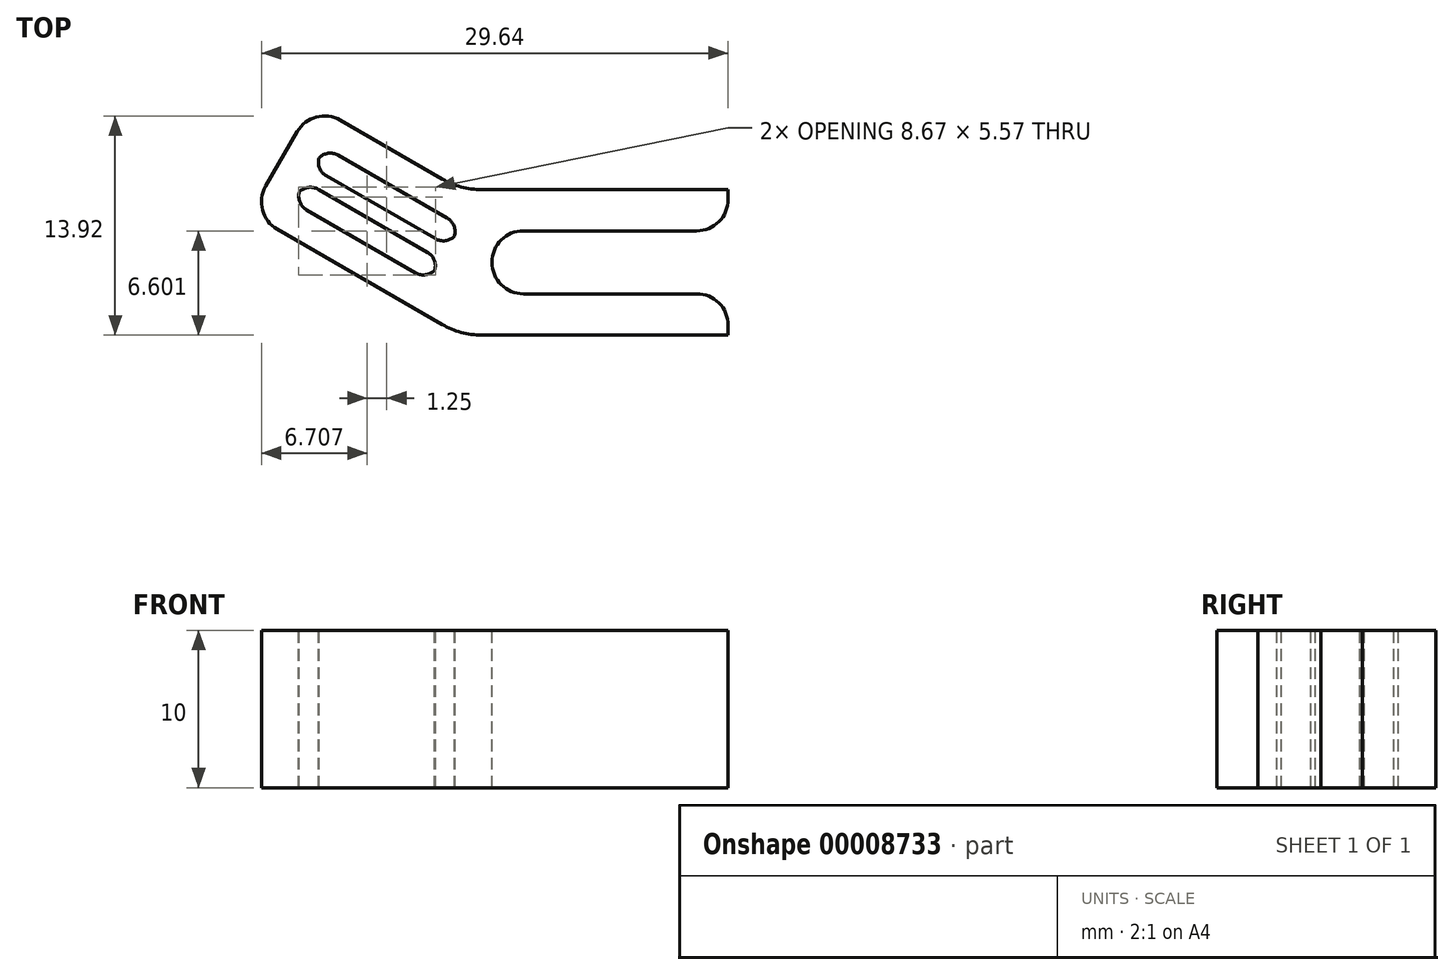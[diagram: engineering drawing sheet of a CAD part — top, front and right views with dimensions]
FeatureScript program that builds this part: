
annotation { "Feature Type Name" : "Feature", "Feature Type Description" : "" }
export const myFeature = defineFeature(function(context is Context, id is Id, definition is map)
    precondition{}
    {
        {
            var Q0;
            Q0=qCreatedBy(makeId("Top.planeOp"),FACE);
            var sketch = newSketch(context, id + "F0", { "sketchPlane" : qUnion([Q0])});
            skLineSegment(sketch, "E0", {"start": v(0, 0) * mm, "end": v(17, 0) * mm});
            skLineSegment(sketch, "E1", {"start": v(17, 0) * mm, "end": v(17, 2.62) * mm});
            skLineSegment(sketch, "E2", {"start": v(17, 2.62) * mm, "end": v(2, 2.62) * mm});
            skLineSegment(sketch, "E3", {"start": v(2, 2.62) * mm, "end": v(2, 6.62) * mm});
            skLineSegment(sketch, "E4", {"start": v(2, 6.62) * mm, "end": v(17, 6.62) * mm});
            skLineSegment(sketch, "E5", {"start": v(17, 6.62) * mm, "end": v(17, 9.24) * mm});
            skLineSegment(sketch, "E6", {"start": v(17, 9.24) * mm, "end": v(0, 9.24) * mm});
            skLineSegment(sketch, "E7", {"start": v(0, 9.24) * mm, "end": v(-9.37, 14.65) * mm});
            skLineSegment(sketch, "E8", {"start": v(-9.37, 14.65) * mm, "end": v(-13.37, 7.72) * mm});
            skLineSegment(sketch, "E9", {"start": v(-13.37, 7.72) * mm, "end": v(0, 0) * mm});
            skLineSegment(sketch, "E10", {"start": v(0.02, 6.92) * mm, "end": v(-8.64, 11.92) * mm});
            skLineSegment(sketch, "E11", {"start": v(-8.64, 11.92) * mm, "end": v(-9.39, 10.62) * mm});
            skLineSegment(sketch, "E12", {"start": v(-9.39, 10.62) * mm, "end": v(-0.73, 5.62) * mm});
            skLineSegment(sketch, "E13", {"start": v(-1.23, 4.75) * mm, "end": v(-9.89, 9.75) * mm});
            skLineSegment(sketch, "E14", {"start": v(-9.89, 9.75) * mm, "end": v(-10.64, 8.45) * mm});
            skLineSegment(sketch, "E15", {"start": v(-10.64, 8.45) * mm, "end": v(-1.98, 3.45) * mm});
            skLineSegment(sketch, "E16", {"start": v(-1.98, 3.45) * mm, "end": v(-1.23, 4.75) * mm});
            skLineSegment(sketch, "E17", {"start": v(-0.73, 5.62) * mm, "end": v(0.02, 6.92) * mm});
            skSolve(sketch);
        }
        {
            var Q0;
            Q0 = qSketchRegion(id + "F0", true);
            extrude(context, id + "F1", {"entities" : qUnion([Q0]), "depth" : 10 * mm});
        }
        {
            var Q0;
            Q0=makeQuery(id+"F1.opExtrude","SWEPT_EDGE",EDGE,{"disambiguationData":[OSD([sQuery(id+"F0.wireOp",EDGE,"22adb448-7b01-4dee-b25c-27ad3b814b58.bottom"),sQuery(id+"F0.wireOp",EDGE,"5c2d3520-68a2-4204-9db6-72b257983ef0")])]});
            var Q1;
            Q1=makeQuery(id+"F1.opExtrude","SWEPT_EDGE",EDGE,{"disambiguationData":[OSD([sQuery(id+"F0.wireOp",EDGE,"22adb448-7b01-4dee-b25c-27ad3b814b58.top"),sQuery(id+"F0.wireOp",EDGE,"5c2d3520-68a2-4204-9db6-72b257983ef0")])]});
            var Q2;
            Q2=makeQuery(id+"F1.opExtrude","SWEPT_EDGE",EDGE,{"disambiguationData":[OSD([sQuery(id+"F0.wireOp",EDGE,"22adb448-7b01-4dee-b25c-27ad3b814b58.bottom"),sQuery(id+"F0.wireOp",EDGE,"22adb448-7b01-4dee-b25c-27ad3b814b58.left")])]});
            var Q3;
            Q3=makeQuery(id+"F1.opExtrude","SWEPT_EDGE",EDGE,{"disambiguationData":[OSD([sQuery(id+"F0.wireOp",EDGE,"22adb448-7b01-4dee-b25c-27ad3b814b58.top"),sQuery(id+"F0.wireOp",EDGE,"22adb448-7b01-4dee-b25c-27ad3b814b58.left")])]});
            var Q4;
            Q4=makeQuery(id+"F1.opExtrude","SWEPT_EDGE",EDGE,{"disambiguationData":[OSD([sQuery(id+"F0.wireOp",EDGE,"E2"),sQuery(id+"F0.wireOp",EDGE,"E3")])]});
            var Q5;
            Q5=makeQuery(id+"F1.opExtrude","SWEPT_EDGE",EDGE,{"disambiguationData":[OSD([sQuery(id+"F0.wireOp",EDGE,"E3"),sQuery(id+"F0.wireOp",EDGE,"E4")])]});
            var Q6;
            Q6=makeQuery(id+"F1.opExtrude","SWEPT_EDGE",EDGE,{"disambiguationData":[OSD([sQuery(id+"F0.wireOp",EDGE,"E1"),sQuery(id+"F0.wireOp",EDGE,"E2")])]});
            var Q7;
            Q7=makeQuery(id+"F1.opExtrude","SWEPT_EDGE",EDGE,{"disambiguationData":[OSD([sQuery(id+"F0.wireOp",EDGE,"E4"),sQuery(id+"F0.wireOp",EDGE,"E5")])]});
            var Q8;
            Q8=makeQuery(id+"F1.opExtrude","SWEPT_EDGE",EDGE,{"disambiguationData":[OSD([sQuery(id+"F0.wireOp",EDGE,"c99527b5-ed65-49ce-9ce6-7f1a6e514e39"),sQuery(id+"F0.wireOp",EDGE,"0ae14092-fb47-4e55-a7a5-957fbf246e4f")])]});
            var Q9;
            Q9=makeQuery(id+"F1.opExtrude","SWEPT_EDGE",EDGE,{"disambiguationData":[OSD([sQuery(id+"F0.wireOp",EDGE,"6eeee744-6f9b-4a90-b979-4488c1a42c6f"),sQuery(id+"F0.wireOp",EDGE,"0ae14092-fb47-4e55-a7a5-957fbf246e4f")])]});
            var Q10;
            Q10=makeQuery(id+"F1.opExtrude","SWEPT_EDGE",EDGE,{"disambiguationData":[OSD([sQuery(id+"F0.wireOp",EDGE,"E7"),sQuery(id+"F0.wireOp",EDGE,"E8")])]});
            var Q11;
            Q11=makeQuery(id+"F1.opExtrude","SWEPT_EDGE",EDGE,{"disambiguationData":[OSD([sQuery(id+"F0.wireOp",EDGE,"E8"),sQuery(id+"F0.wireOp",EDGE,"E9")])]});
            fillet(context, id + "F2", {"entities" : qUnion([Q0, Q1, Q2, Q3, Q4, Q5, Q6, Q7, Q8, Q9, Q10, Q11]), "radius" : 2 * mm, "tangentPropagation" : true, "allowEdgeOverflow" : false});
        }
        {
            var Q0;
            Q0=makeQuery(id+"F1.opExtrude","SWEPT_EDGE",EDGE,{"disambiguationData":[OSD([sQuery(id+"F0.wireOp",EDGE,"E14"),sQuery(id+"F0.wireOp",EDGE,"E15")])]});
            var Q1;
            Q1=makeQuery(id+"F1.opExtrude","SWEPT_EDGE",EDGE,{"disambiguationData":[OSD([sQuery(id+"F0.wireOp",EDGE,"E11"),sQuery(id+"F0.wireOp",EDGE,"E12")])]});
            var Q2;
            Q2=makeQuery(id+"F1.opExtrude","SWEPT_EDGE",EDGE,{"disambiguationData":[OSD([sQuery(id+"F0.wireOp",EDGE,"E15"),sQuery(id+"F0.wireOp",EDGE,"E16")])]});
            var Q3;
            Q3=makeQuery(id+"F1.opExtrude","SWEPT_EDGE",EDGE,{"disambiguationData":[OSD([sQuery(id+"F0.wireOp",EDGE,"E12"),sQuery(id+"F0.wireOp",EDGE,"E17")])]});
            var Q4;
            Q4=makeQuery(id+"F1.opExtrude","SWEPT_EDGE",EDGE,{"disambiguationData":[OSD([sQuery(id+"F0.wireOp",EDGE,"E13"),sQuery(id+"F0.wireOp",EDGE,"E16")])]});
            var Q5;
            Q5=makeQuery(id+"F1.opExtrude","SWEPT_EDGE",EDGE,{"disambiguationData":[OSD([sQuery(id+"F0.wireOp",EDGE,"E10"),sQuery(id+"F0.wireOp",EDGE,"E11")])]});
            var Q6;
            Q6=makeQuery(id+"F1.opExtrude","SWEPT_EDGE",EDGE,{"disambiguationData":[OSD([sQuery(id+"F0.wireOp",EDGE,"E13"),sQuery(id+"F0.wireOp",EDGE,"E14")])]});
            var Q7;
            Q7=makeQuery(id+"F1.opExtrude","SWEPT_EDGE",EDGE,{"disambiguationData":[OSD([sQuery(id+"F0.wireOp",EDGE,"E10"),sQuery(id+"F0.wireOp",EDGE,"E17")])]});
            fillet(context, id + "F3", {"entities" : qUnion([Q0, Q1, Q2, Q3, Q4, Q5, Q6, Q7]), "radius" : 1 * mm, "tangentPropagation" : true, "allowEdgeOverflow" : false});
        }
        {
            var Q0;
            Q0=makeQuery(id+"F1.opExtrude","SWEPT_EDGE",EDGE,{"disambiguationData":[OSD([sQuery(id+"F0.wireOp",EDGE,"E6"),sQuery(id+"F0.wireOp",EDGE,"E7")])]});
            var Q1;
            Q1=makeQuery(id+"F1.opExtrude","SWEPT_EDGE",EDGE,{"disambiguationData":[OSD([sQuery(id+"F0.wireOp",EDGE,"E0"),sQuery(id+"F0.wireOp",EDGE,"E9")])]});
            fillet(context, id + "F4", {"entities" : qUnion([Q0, Q1]), "radius" : 5 * mm, "tangentPropagation" : true, "allowEdgeOverflow" : false});
        }
    });
